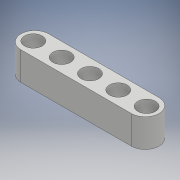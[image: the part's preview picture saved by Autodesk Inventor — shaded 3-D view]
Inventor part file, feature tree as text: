
AUTODESK INVENTOR PART (.ipt)
format: ipt  version: 2018.2 (Build 222227000, 227)  size: 132,608 bytes
history: native  units: mm
features: fillet x4, extrude x2, sketch x2
ambient origin geometry x8: Origin, YZ Plane, XZ Plane, XY Plane, X Axis, Y Axis, Z Axis, Center Point
bodies: Solid1 (feature_tree)
feature tree (8):
  extrude  "Extrusion1"  Depth=7.8mm
  fillet  "Fillet1"  Radius=8.0mm
  fillet  "Fillet2"  Radius=3.9mm
  fillet  "Fillet3"  Radius=3.9mm
  fillet  "Fillet4"  Radius=3.9mm
  extrude  "Extrusion2"  Depth=39.0mm
  sketch  "Sketch1"  dims[d0=39.0mm d1=7.8mm d2=8.0mm d3=0.0mm d4=3.9mm d5=3.9mm d6=3.9mm]
  sketch  "Sketch2"  dims[d7=3.9mm d16=39.0mm d17=5.0mm d18=5.0mm d19=5.0mm d20=5.0mm d21=5.0mm d24=3.0mm d25=3.0mm d27=3.0mm d28=3.0mm d29=8.0mm d30=0.0mm]
